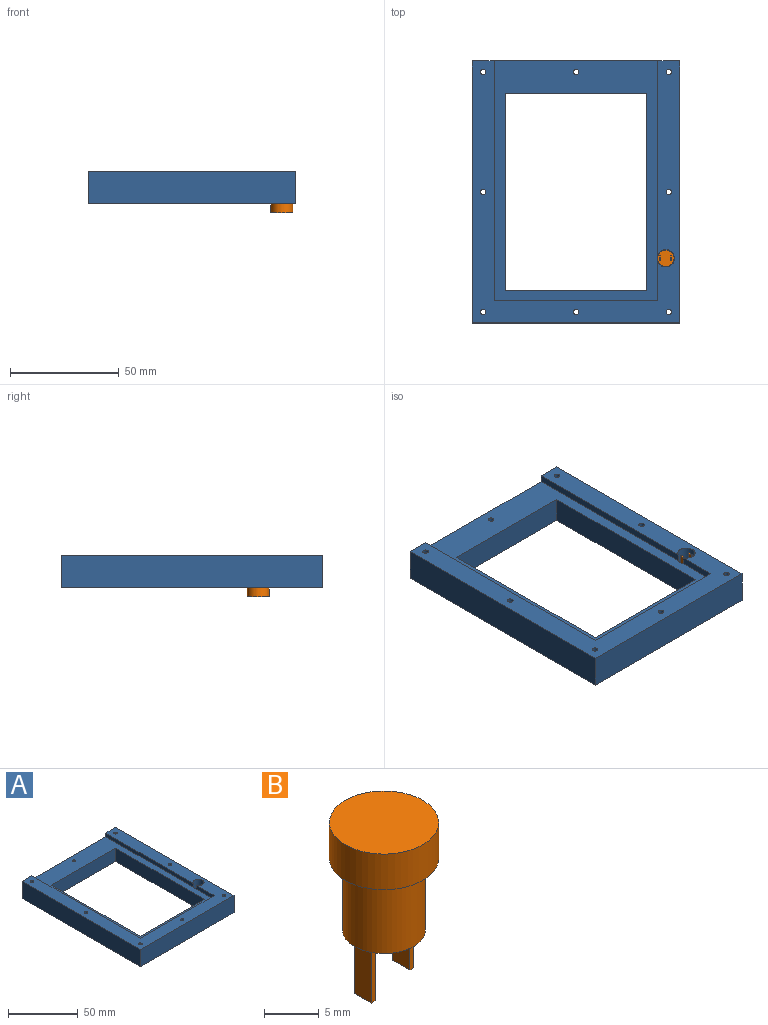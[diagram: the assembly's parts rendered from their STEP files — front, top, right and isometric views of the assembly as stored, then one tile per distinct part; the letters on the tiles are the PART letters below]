
ASSEMBLY  parts=2 mates=1
PART A: 24 faces, bbox 95.3x120.3x15 mm
  f0: plane 89.07x3.3mm, normal (-1,0,0), area 293.9mm2, adj f2,f4,f7,f23
  f1: plane 120.3x95.3mm, normal (0,0,-1), area 5494mm2, adj f3,f4,f5,f6,f11,f12,f13,f14
  f2: plane 110.2x75.1mm, normal (0,0,1), area 2389.5mm2, adj f0,f4,f8,f9,f10,f11,f12,f13
  f3: plane 120.3x15mm, normal (1,0,0), area 1804.5mm2, adj f1,f4,f6,f7
  f4: plane 95.3x15mm, normal (0,1,0), area 1181.7mm2, adj f0,f1,f2,f3,f5,f7,f9
  f5: plane 120.3x15mm, normal (-1,0,0), area 1804.5mm2, adj f1,f4,f6,f7
  f6: plane 95.3x15mm, normal (0,-1,0), area 1429.5mm2, adj f1,f3,f5,f7
  f7: plane 120.3x95.3mm, normal (0,0,1), area 3104.5mm2, adj f0,f3,f4,f5,f6,f8,f9,f10
  f8: plane 18.11x3.3mm, normal (-1,0,0), area 59.8mm2, adj f2,f7,f10,f23
  f9: plane 110.2x3.3mm, normal (1,0,0), area 363.7mm2, adj f2,f4,f7,f10
  f10: plane 75.1x3.3mm, normal (0,1,0), area 247.8mm2, adj f2,f7,f8,f9
  f11: plane 65.2x11.7mm, normal (0,1,0), area 762.8mm2, adj f1,f2,f12,f14
  f12: plane 90.2x11.7mm, normal (-1,0,0), area 1055.3mm2, adj f1,f2,f11,f13
  f13: plane 65.2x11.7mm, normal (0,-1,0), area 762.8mm2, adj f1,f2,f12,f14
  f14: plane 90.2x11.7mm, normal (1,0,0), area 1055.3mm2, adj f1,f2,f11,f13
  f15: cylinder r=1.25mm len=15mm, axis (0,0,1), area 117.8mm2, adj f1,f7
  f16: cylinder r=1.25mm len=15mm, axis (0,0,1), area 117.8mm2, adj f1,f7
  f17: cylinder r=1.25mm len=15mm, axis (0,0,1), area 117.8mm2, adj f1,f7
  f18: cylinder r=1.25mm len=15mm, axis (0,0,1), area 117.8mm2, adj f1,f7
  f19: cylinder r=1.25mm len=15mm, axis (0,0,1), area 117.8mm2, adj f1,f7
  f20: cylinder r=1.25mm len=15mm, axis (0,0,1), area 117.8mm2, adj f1,f7
  f21: cylinder r=1.25mm len=15mm, axis (0,0,1), area 117.8mm2, adj f1,f7
  f22: cylinder r=1.25mm len=11.7mm, axis (0,0,1), area 91.9mm2, adj f1,f2
  f23: cylinder r=4mm len=15mm, axis (0,0,1), area 366.7mm2, adj f0,f1,f2,f7,f8
PART B: 15 faces, bbox 10x10x18.3 mm
  f0: plane 7.6x7.6mm, normal (0,0,-1), area 43.2mm2, adj f2,f5,f7,f8,f9,f10,f12,f13
  f1: plane 10x10mm, normal (0,0,1), area 78.5mm2, adj f4
  f2: cylinder r=3.8mm len=8mm, axis (0,0,-1), area 191mm2, adj f0,f3
  f3: plane 10x10mm, normal (0,0,-1), area 33.2mm2, adj f2,f4
  f4: cylinder r=5mm len=10mm, axis (0,0,-1), area 125.7mm2, adj f1,f3
  f5: plane 6.3x2.2mm, normal (-1,0,0), area 13.9mm2, adj f0,f6,f8,f9
  f6: plane 2.2x0.5mm, normal (0,0,-1), area 1.1mm2, adj f5,f7,f8,f9
  f7: plane 6.3x2.2mm, normal (1,0,0), area 13.9mm2, adj f0,f6,f8,f9
  f8: plane 6.3x0.5mm, normal (0,-1,0), area 3.1mm2, adj f0,f5,f6,f7
  f9: plane 6.3x0.5mm, normal (0,1,0), area 3.1mm2, adj f0,f5,f6,f7
  f10: plane 5.1x2.2mm, normal (-1,0,0), area 11.2mm2, adj f0,f11,f13,f14
  f11: plane 2.2x0.5mm, normal (0,0,-1), area 1.1mm2, adj f10,f12,f13,f14
  f12: plane 5.1x2.2mm, normal (1,0,0), area 11.2mm2, adj f0,f11,f13,f14
  f13: plane 5.1x0.5mm, normal (0,-1,0), area 2.5mm2, adj f0,f10,f11,f12
  f14: plane 5.1x0.5mm, normal (0,1,0), area 2.5mm2, adj f0,f10,f11,f12
PLACE A at identity fixed
PLACE B rot(axis=(1,0,0),180deg) t=(41.25,-30.43,-15)mm
MATE fastened B.f2 <-> A.f23  axis (0,0,1) through (41.25,-30.43,-15)mm
